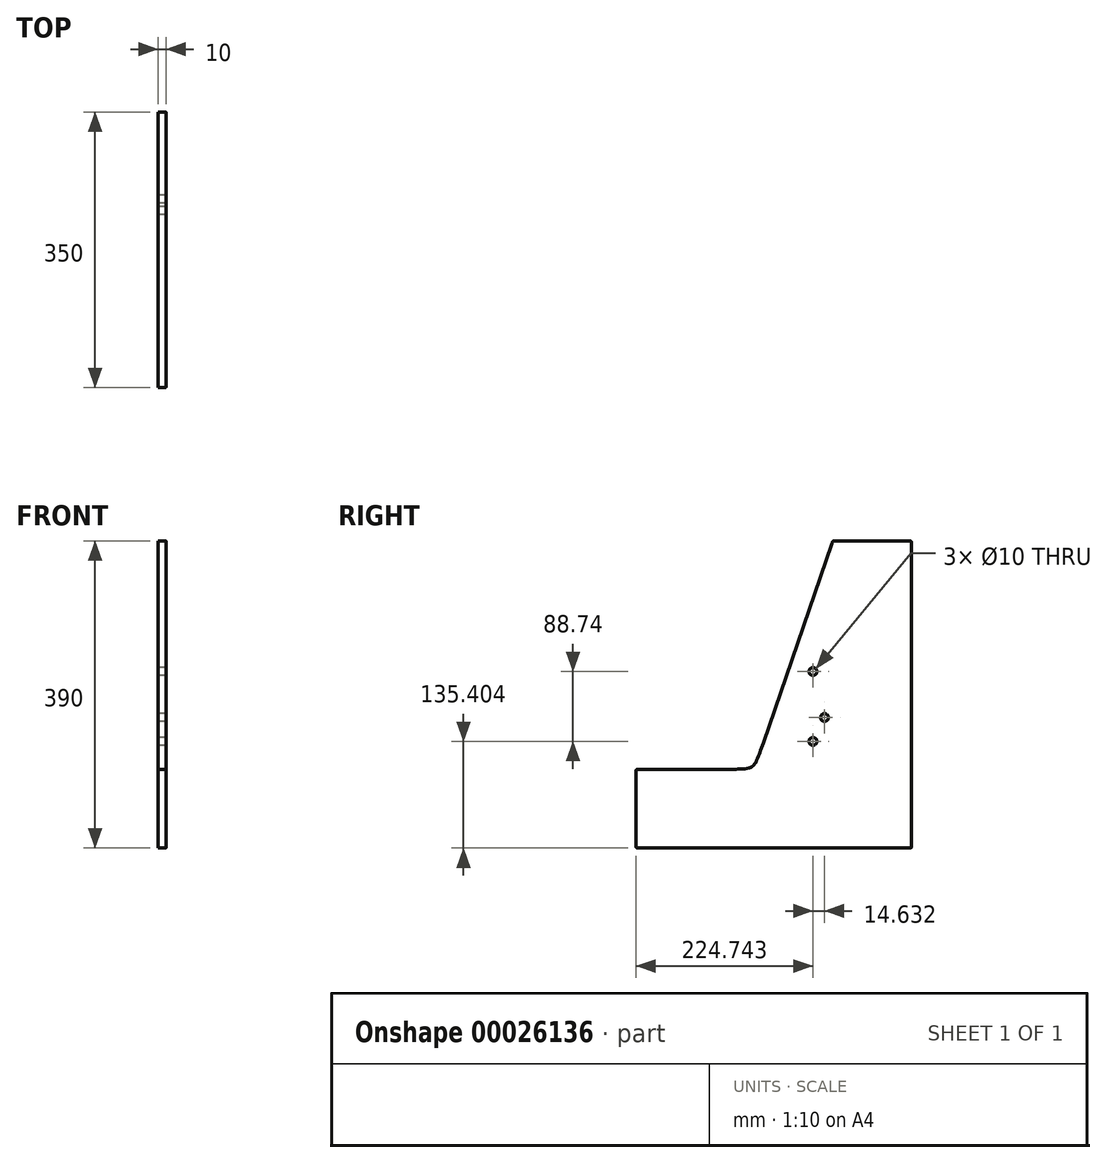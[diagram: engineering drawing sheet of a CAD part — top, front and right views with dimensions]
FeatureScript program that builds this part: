
annotation { "Feature Type Name" : "Feature", "Feature Type Description" : "" }
export const myFeature = defineFeature(function(context is Context, id is Id, definition is map)
    precondition{}
    {
        {
            var Q0;
            Q0=qCreatedBy(makeId("Right.planeOp"),FACE);
            var sketch = newSketch(context, id + "F0", { "sketchPlane" : qUnion([Q0])});
            skLineSegment(sketch, "E0.rect.bottom", {"start": v(175, -195) * mm, "end": v(-175, -195) * mm});
            skLineSegment(sketch, "E0.rect.top", {"start": v(175, 195) * mm, "end": v(75, 195) * mm});
            skLineSegment(sketch, "E0.rect.left", {"start": v(175, -195) * mm, "end": v(175, 195) * mm});
            skLineSegment(sketch, "E0.rect.right", {"start": v(-175, -195) * mm, "end": v(-175, -95) * mm});
            skPoint(sketch, "E0.rect.middle", {"position": v(0, 0) * mm});
            skLineSegment(sketch, "E1", {"start": v(49.74, 195) * mm, "end": v(49.74, -195) * mm, "construction": true});
            skCircle(sketch, "E2", {"center": v(49.74, -59.6) * mm, "radius": 5 * mm});
            skCircle(sketch, "E3", {"center": v(49.74, 29.14) * mm, "radius": 5 * mm});
            skCircle(sketch, "E4", {"center": v(64.38, -29.28) * mm, "radius": 5 * mm});
            skLineSegment(sketch, "E5", {"start": v(75, 195) * mm, "end": v(-25, -95) * mm});
            skLineSegment(sketch, "E6", {"start": v(-25, -95) * mm, "end": v(-175, -95) * mm});
            skPoint(sketch, "E7.orphan", {"position": v(-175, 195) * mm});
            skSolve(sketch);
        }
        {
            var Q0;
            Q0=makeQuery(id+"F0.imprint","IMPRINT",FACE,{"disambiguationData":[TD([[makeQuery(id+"F0.imprint","IMPRINT",EDGE,{"derivedFrom":sQuery(id+"F0.wireOp",EDGE,"E0.rect.bottom")}),-1.0]])]});
            extrude(context, id + "F1", {"entities" : qUnion([Q0]), "depth" : 10 * mm});
        }
        {
            var Q0;
            Q0=makeQuery(id+"F1.opExtrude","SWEPT_EDGE",EDGE,{"disambiguationData":[OSD([sQuery(id+"F0.wireOp",EDGE,"E0.rect.bottom"),sQuery(id+"F0.wireOp",EDGE,"E0.rect.left")])]});
            var Q1;
            Q1=makeQuery(id+"F1.opExtrude","SWEPT_EDGE",EDGE,{"disambiguationData":[OSD([sQuery(id+"F0.wireOp",EDGE,"E0.rect.top"),sQuery(id+"F0.wireOp",EDGE,"E0.rect.left")])]});
            var Q2;
            Q2=makeQuery(id+"F1.opExtrude","SWEPT_EDGE",EDGE,{"disambiguationData":[OSD([sQuery(id+"F0.wireOp",EDGE,"E0.rect.top"),sQuery(id+"F0.wireOp",EDGE,"E5")])]});
            var Q3;
            Q3=makeQuery(id+"F1.opExtrude","SWEPT_EDGE",EDGE,{"disambiguationData":[OSD([sQuery(id+"F0.wireOp",EDGE,"E0.rect.right"),sQuery(id+"F0.wireOp",EDGE,"E6")])]});
            var Q4;
            Q4=makeQuery(id+"F1.opExtrude","SWEPT_EDGE",EDGE,{"disambiguationData":[OSD([sQuery(id+"F0.wireOp",EDGE,"E0.rect.bottom"),sQuery(id+"F0.wireOp",EDGE,"E0.rect.right")])]});
            fillet(context, id + "F2", {"entities" : qUnion([Q0, Q1, Q2, Q3, Q4]), "radius" : 5 * mm, "tangentPropagation" : true, "rho" : 0.8, "crossSection" : FilletCrossSection.CONIC, "allowEdgeOverflow" : false});
        }
        {
            var Q0;
            Q0=makeQuery(id+"F1.opExtrude","SWEPT_EDGE",EDGE,{"disambiguationData":[OSD([sQuery(id+"F0.wireOp",EDGE,"E5"),sQuery(id+"F0.wireOp",EDGE,"E6")])]});
            fillet(context, id + "F3", {"entities" : qUnion([Q0]), "radius" : 50 * mm, "tangentPropagation" : true, "rho" : 0.8, "crossSection" : FilletCrossSection.CONIC, "allowEdgeOverflow" : false});
        }
    });
